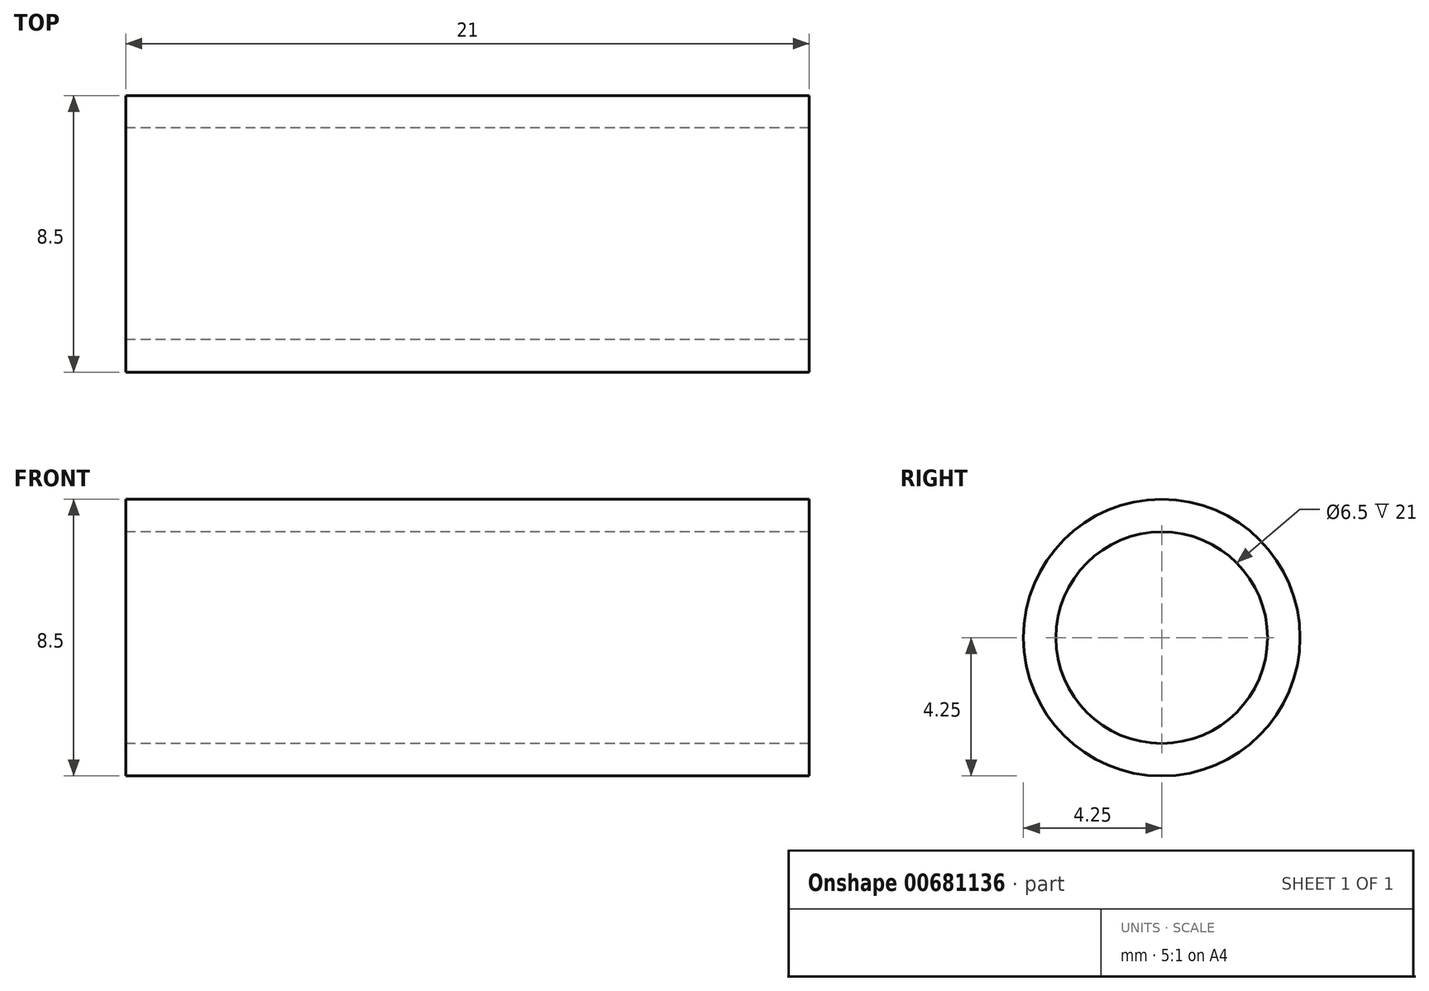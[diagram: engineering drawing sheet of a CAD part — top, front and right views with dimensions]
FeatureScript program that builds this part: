
annotation { "Feature Type Name" : "Feature", "Feature Type Description" : "" }
export const myFeature = defineFeature(function(context is Context, id is Id, definition is map)
    precondition{}
    {
        {
            var Q0;
            Q0=qCreatedBy(makeId("Right.planeOp"),FACE);
            var sketch = newSketch(context, id + "F0", { "sketchPlane" : qUnion([Q0])});
            skCircle(sketch, "E0", {"center": v(0, 0) * mm, "radius": 4.25 * mm});
            skPoint(sketch, "E1", {"position": v(4.25, 0) * mm});
            skSolve(sketch);
        }
        {
            var Q0;
            Q0=qSketchRegion(id+"F0",true);
            extrude(context, id + "F1", {"entities" : qUnion([Q0]), "depth" : 21 * mm, "offsetDistance" : 25 * mm});
        }
        {
            var Q0;
            Q0=qCreatedBy(makeId("Right.planeOp"),FACE);
            var sketch = newSketch(context, id + "F2", { "sketchPlane" : qUnion([Q0])});
            skCircle(sketch, "E2", {"center": v(0, 0) * mm, "radius": 4.25 * mm});
            skSolve(sketch);
        }
        {
            var Q0;
            Q0=qSketchRegion(id+"F2",true);
            var Q1;
            Q1=qSketchRegion(id+"F4",true);
            extrude(context, id + "F3", {"entities" : qUnion([Q0, Q1]), "operationType" : NewBodyOperationType.ADD, "depth" : 21 * mm});
        }
        {
            var Q0;
            Q0=makeQuery(id+"F0.imprint","IMPRINT",FACE,{"disambiguationData":[TD([[makeQuery(id+"F0.imprint","IMPRINT",EDGE,{"derivedFrom":sQuery(id+"F0.wireOp",EDGE,"E0")}),1.0]])]});
            var sketch = newSketch(context, id + "F4", { "sketchPlane" : qUnion([Q0])});
            skCircle(sketch, "E3", {"center": v(0, 0) * mm, "radius": 4.2 * mm});
            skSolve(sketch);
        }
        {
            var Q0;
            Q0=sQuery(id+"F4.wireOp",VERTEX,"E3.center");
            var Q1;
            Q1=makeQuery(id+"F1.opExtrude","SWEPT_BODY",BODY,{"disambiguationData":[OSD([sQuery(id+"F0.wireOp",EDGE,"E0")])]});
            hole(context, id + "F5", {"style" : HoleStyle.SIMPLE, "endStyle" : HoleEndStyle.THROUGH, "oppositeDirection" : true, "holeDiameter" : 8.4 * mm, "isTappedThrough" : true, "tappedDepth" : 12 * mm, "tapClearance" : 3, "locations" : qUnion([Q0]), "scope" : qUnion([Q1])});
        }
        {
            var Q0;
            Q0=qCreatedBy(makeId("Right.planeOp"),FACE);
            var sketch = newSketch(context, id + "F6", { "sketchPlane" : qUnion([Q0])});
            skCircle(sketch, "E4", {"center": v(0, 0) * mm, "radius": 3.25 * mm});
            skSolve(sketch);
        }
        {
            var Q0;
            Q0=qSketchRegion(id+"F4",true);
            extrude(context, id + "F7", {"entities" : qUnion([Q0]), "operationType" : NewBodyOperationType.ADD, "depth" : 21 * mm});
        }
        {
            var Q0;
            Q0=sQuery(id+"F6.wireOp",VERTEX,"E4.center");
            var Q1;
            Q1=makeQuery(id+"F1.opExtrude","SWEPT_BODY",BODY,{"disambiguationData":[OSD([sQuery(id+"F0.wireOp",EDGE,"E0")])]});
            hole(context, id + "F8", {"style" : HoleStyle.SIMPLE, "endStyle" : HoleEndStyle.THROUGH, "oppositeDirection" : true, "holeDiameter" : 6.5 * mm, "isTappedThrough" : true, "tappedDepth" : 12 * mm, "tapClearance" : 3, "locations" : qUnion([Q0]), "scope" : qUnion([Q1]), "majorDiameter" : 5 * mm});
        }
    });
